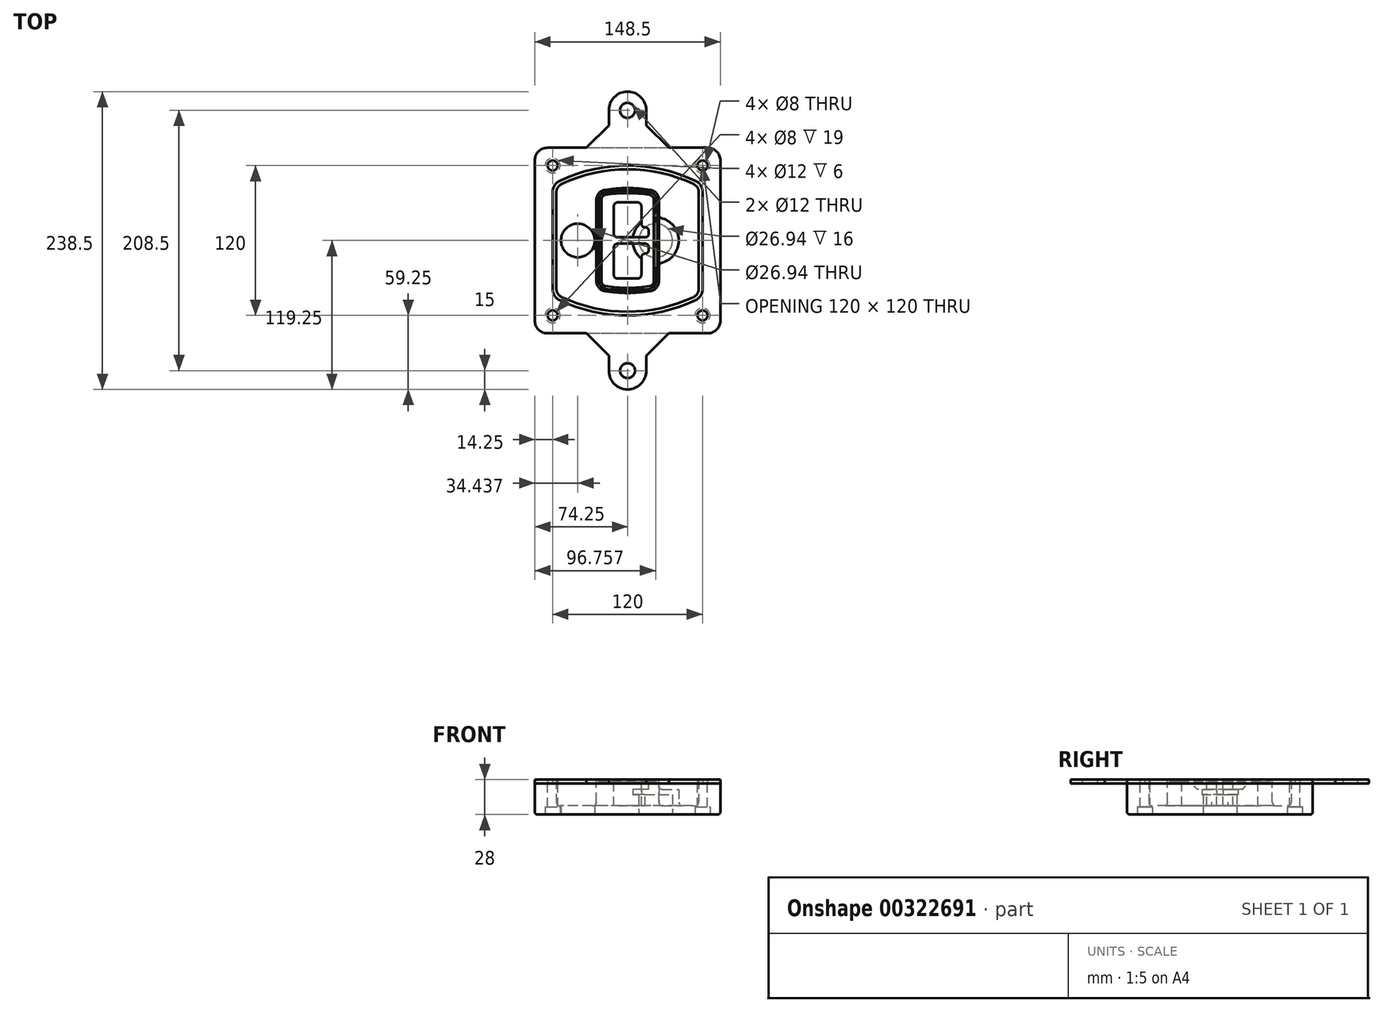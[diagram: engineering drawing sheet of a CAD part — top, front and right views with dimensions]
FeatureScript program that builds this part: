
annotation { "Feature Type Name" : "Feature", "Feature Type Description" : "" }
export const myFeature = defineFeature(function(context is Context, id is Id, definition is map)
    precondition{}
    {
        {
            var Q0;
            Q0=qCreatedBy(makeId("Top.planeOp"),FACE);
            var sketch = newSketch(context, id + "F0", { "sketchPlane" : qUnion([Q0])});
            skPoint(sketch, "E0.rect.middle", {"position": v(0, 0) * mm});
            skLineSegment(sketch, "E1.bottom", {"start": v(-64.25, -74.25) * mm, "end": v(64.25, -74.25) * mm});
            skLineSegment(sketch, "E1.top", {"start": v(-64.25, 74.25) * mm, "end": v(64.25, 74.25) * mm});
            skLineSegment(sketch, "E1.left", {"start": v(-74.25, -64.25) * mm, "end": v(-74.25, 64.25) * mm});
            skLineSegment(sketch, "E1.right", {"start": v(74.25, -64.25) * mm, "end": v(74.25, 64.25) * mm});
            skLineSegment(sketch, "E2", {"start": v(-74.25, 74.25) * mm, "end": v(74.25, -74.25) * mm, "construction": true});
            skLineSegment(sketch, "E3", {"start": v(74.25, 74.25) * mm, "end": v(-74.25, -74.25) * mm, "construction": true});
            skCircle(sketch, "E4", {"center": v(-60, 60) * mm, "radius": 4 * mm});
            skCircle(sketch, "E5", {"center": v(60, 60) * mm, "radius": 4 * mm});
            skCircle(sketch, "E6", {"center": v(60, -60) * mm, "radius": 4 * mm});
            skCircle(sketch, "E7", {"center": v(-60, -60) * mm, "radius": 4 * mm});
            skLineSegment(sketch, "E8", {"start": v(-60, 60) * mm, "end": v(60, 60) * mm, "construction": true});
            skLineSegment(sketch, "E9", {"start": v(60, 60) * mm, "end": v(60, -60) * mm, "construction": true});
            skLineSegment(sketch, "E10", {"start": v(60, -60) * mm, "end": v(-60, -60) * mm, "construction": true});
            skLineSegment(sketch, "E11", {"start": v(-60, -60) * mm, "end": v(-60, 60) * mm, "construction": true});
            skLineSegment(sketch, "E12", {"start": v(-60, 38.83) * mm, "end": v(-60, -38.83) * mm});
            skLineSegment(sketch, "E13", {"start": v(60, 38.83) * mm, "end": v(60, -38.83) * mm});
            skArc(sketch, "E14", {"start": v(54.26, 47.88) * mm, "mid": v(0, 60) * mm, "end": v(-54.26, 47.88) * mm});
            skArc(sketch, "E15", {"start": v(-54.26, -47.88) * mm, "mid": v(0, -60) * mm, "end": v(54.26, -47.88) * mm});
            skLineSegment(sketch, "E16", {"start": v(-60, 0) * mm, "end": v(60, 0) * mm, "construction": true});
            skPoint(sketch, "E17.visualSharp", {"position": v(-60, -45) * mm});
            skArc(sketch, "E17.filletArc", {"start": v(-60, -38.83) * mm, "mid": v(-58.44, -44.2) * mm, "end": v(-54.26, -47.88) * mm});
            skPoint(sketch, "E18.visualSharp", {"position": v(-60, 45) * mm});
            skArc(sketch, "E18.filletArc", {"start": v(-54.26, 47.88) * mm, "mid": v(-58.44, 44.2) * mm, "end": v(-60, 38.83) * mm});
            skPoint(sketch, "E19.visualSharp", {"position": v(60, 45) * mm});
            skArc(sketch, "E19.filletArc", {"start": v(60, 38.83) * mm, "mid": v(58.44, 44.2) * mm, "end": v(54.26, 47.88) * mm});
            skPoint(sketch, "E20.visualSharp", {"position": v(60, -45) * mm});
            skArc(sketch, "E20.filletArc", {"start": v(54.26, -47.88) * mm, "mid": v(58.44, -44.2) * mm, "end": v(60, -38.83) * mm});
            skPoint(sketch, "E21.visualSharp", {"position": v(-74.25, 74.25) * mm});
            skArc(sketch, "E21.filletArc", {"start": v(-64.25, 74.25) * mm, "mid": v(-71.32, 71.32) * mm, "end": v(-74.25, 64.25) * mm});
            skPoint(sketch, "E22.visualSharp", {"position": v(74.25, 74.25) * mm});
            skArc(sketch, "E22.filletArc", {"start": v(74.25, 64.25) * mm, "mid": v(71.32, 71.32) * mm, "end": v(64.25, 74.25) * mm});
            skPoint(sketch, "E23.visualSharp", {"position": v(74.25, -74.25) * mm});
            skArc(sketch, "E23.filletArc", {"start": v(64.25, -74.25) * mm, "mid": v(71.32, -71.32) * mm, "end": v(74.25, -64.25) * mm});
            skPoint(sketch, "E24.visualSharp", {"position": v(-74.25, -74.25) * mm});
            skArc(sketch, "E24.filletArc", {"start": v(-74.25, -64.25) * mm, "mid": v(-71.32, -71.32) * mm, "end": v(-64.25, -74.25) * mm});
            skArc(sketch, "E25.0", {"start": v(57, 38.83) * mm, "mid": v(55.9, 42.58) * mm, "end": v(52.98, 45.17) * mm});
            skLineSegment(sketch, "E25.1", {"start": v(57, 38.83) * mm, "end": v(57, -38.83) * mm});
            skArc(sketch, "E25.2", {"start": v(52.98, -45.17) * mm, "mid": v(55.9, -42.58) * mm, "end": v(57, -38.83) * mm});
            skArc(sketch, "E25.3", {"start": v(-52.98, -45.17) * mm, "mid": v(0, -57) * mm, "end": v(52.98, -45.17) * mm});
            skArc(sketch, "E25.4", {"start": v(-57, -38.83) * mm, "mid": v(-55.9, -42.58) * mm, "end": v(-52.98, -45.17) * mm});
            skArc(sketch, "E25.5", {"start": v(52.98, 45.17) * mm, "mid": v(0, 57) * mm, "end": v(-52.98, 45.17) * mm});
            skLineSegment(sketch, "E25.6", {"start": v(-57, 38.83) * mm, "end": v(-57, -38.83) * mm});
            skArc(sketch, "E25.7", {"start": v(-52.98, 45.17) * mm, "mid": v(-55.9, 42.58) * mm, "end": v(-57, 38.83) * mm});
            skArc(sketch, "E26.0", {"start": v(-55.96, 51.5) * mm, "mid": v(-61.82, 46.33) * mm, "end": v(-64, 38.83) * mm});
            skArc(sketch, "E26.1", {"start": v(55.96, 51.5) * mm, "mid": v(0, 64) * mm, "end": v(-55.96, 51.5) * mm});
            skArc(sketch, "E26.2", {"start": v(64, 38.83) * mm, "mid": v(61.82, 46.33) * mm, "end": v(55.96, 51.5) * mm});
            skLineSegment(sketch, "E26.3", {"start": v(64, 38.83) * mm, "end": v(64, -38.83) * mm});
            skArc(sketch, "E26.4", {"start": v(55.96, -51.5) * mm, "mid": v(61.82, -46.33) * mm, "end": v(64, -38.83) * mm});
            skLineSegment(sketch, "E26.5", {"start": v(-64, 38.83) * mm, "end": v(-64, -38.83) * mm});
            skArc(sketch, "E26.6", {"start": v(-55.96, -51.5) * mm, "mid": v(0, -64) * mm, "end": v(55.96, -51.5) * mm});
            skArc(sketch, "E26.7", {"start": v(-64, -38.83) * mm, "mid": v(-61.82, -46.33) * mm, "end": v(-55.96, -51.5) * mm});
            skSolve(sketch);
        }
        {
            var Q0;
            Q0=makeQuery(id+"F0.imprint","IMPRINT",FACE,{"disambiguationData":[TD([[makeQuery(id+"F0.imprint","IMPRINT",EDGE,{"derivedFrom":sQuery(id+"F0.wireOp",EDGE,"E1.bottom")}),1.0]])]});
            var Q1;
            Q1=makeQuery(id+"F0.imprint","IMPRINT",FACE,{"disambiguationData":[TD([[makeQuery(id+"F0.imprint","IMPRINT",EDGE,{"derivedFrom":sQuery(id+"F0.wireOp",EDGE,"E12")}),1.0]])]});
            var Q2;
            Q2=makeQuery(id+"F0.imprint","IMPRINT",FACE,{"disambiguationData":[TD([[makeQuery(id+"F0.imprint","IMPRINT",EDGE,{"derivedFrom":sQuery(id+"F0.wireOp",EDGE,"E25.0")}),1.0]])]});
            var Q3;
            Q3=makeQuery(id+"F0.imprint","IMPRINT",FACE,{"disambiguationData":[TD([[makeQuery(id+"F0.imprint","IMPRINT",EDGE,{"derivedFrom":sQuery(id+"F0.wireOp",EDGE,"E12")}),-1.0]])]});
            extrude(context, id + "F1", {"entities" : qUnion([Q0, Q1, Q2, Q3]), "oppositeDirection" : true, "depth" : 25 * mm});
        }
        {
            var Q0;
            Q0=makeQuery(id+"F0.imprint","IMPRINT",FACE,{"disambiguationData":[TD([[makeQuery(id+"F0.imprint","IMPRINT",EDGE,{"derivedFrom":sQuery(id+"F0.wireOp",EDGE,"E12")}),1.0]])]});
            extrude(context, id + "F2", {"entities" : qUnion([Q0]), "operationType" : NewBodyOperationType.ADD, "depth" : 3 * mm});
        }
        {
            var Q0;
            Q0=makeQuery(id+"F0.imprint","IMPRINT",FACE,{"disambiguationData":[TD([[makeQuery(id+"F0.imprint","IMPRINT",EDGE,{"derivedFrom":sQuery(id+"F0.wireOp",EDGE,"E25.0")}),1.0]])]});
            extrude(context, id + "F3", {"entities" : qUnion([Q0]), "operationType" : NewBodyOperationType.REMOVE, "oppositeDirection" : true, "depth" : 18 * mm});
        }
        {
            var Q0;
            Q0=makeQuery(id+"F2.opExtrude","CAP_FACE",FACE,{"disambiguationData":[OSD([sQuery(id+"F0.wireOp",EDGE,"E12"),sQuery(id+"F0.wireOp",EDGE,"E13"),sQuery(id+"F0.wireOp",EDGE,"E14"),sQuery(id+"F0.wireOp",EDGE,"E15"),sQuery(id+"F0.wireOp",EDGE,"E17.filletArc"),sQuery(id+"F0.wireOp",EDGE,"E18.filletArc"),sQuery(id+"F0.wireOp",EDGE,"E19.filletArc"),sQuery(id+"F0.wireOp",EDGE,"E20.filletArc"),sQuery(id+"F0.wireOp",EDGE,"E25.0"),sQuery(id+"F0.wireOp",EDGE,"E25.1"),sQuery(id+"F0.wireOp",EDGE,"E25.2"),sQuery(id+"F0.wireOp",EDGE,"E25.3"),sQuery(id+"F0.wireOp",EDGE,"E25.4"),sQuery(id+"F0.wireOp",EDGE,"E25.5"),sQuery(id+"F0.wireOp",EDGE,"E25.6"),sQuery(id+"F0.wireOp",EDGE,"E25.7")])],"isStart":false});
            var sketch = newSketch(context, id + "F4", { "sketchPlane" : qUnion([Q0])});
            skArc(sketch, "E27.0", {"start": v(-18.34, -40.45) * mm, "mid": v(0, -42) * mm, "end": v(18.34, -40.45) * mm});
            skArc(sketch, "E28.0", {"start": v(18.34, 40.45) * mm, "mid": v(0, 42) * mm, "end": v(-18.34, 40.45) * mm});
            skLineSegment(sketch, "E29", {"start": v(-25, 32.57) * mm, "end": v(-25, -32.57) * mm});
            skLineSegment(sketch, "E30", {"start": v(25, 32.57) * mm, "end": v(25, -32.57) * mm});
            skLineSegment(sketch, "E31", {"start": v(-25, 39.1) * mm, "end": v(25, 39.1) * mm, "construction": true});
            skLineSegment(sketch, "E32", {"start": v(-25, -39.1) * mm, "end": v(25, -39.1) * mm, "construction": true});
            skPoint(sketch, "E33.visualSharp", {"position": v(-25, 39.1) * mm});
            skArc(sketch, "E33.filletArc", {"start": v(-18.34, 40.45) * mm, "mid": v(-23.11, 37.73) * mm, "end": v(-25, 32.57) * mm});
            skPoint(sketch, "E34.visualSharp", {"position": v(25, 39.1) * mm});
            skArc(sketch, "E34.filletArc", {"start": v(25, 32.57) * mm, "mid": v(23.11, 37.73) * mm, "end": v(18.34, 40.45) * mm});
            skPoint(sketch, "E35.visualSharp", {"position": v(25, -39.1) * mm});
            skArc(sketch, "E35.filletArc", {"start": v(18.34, -40.45) * mm, "mid": v(23.11, -37.73) * mm, "end": v(25, -32.57) * mm});
            skPoint(sketch, "E36.visualSharp", {"position": v(-25, -39.1) * mm});
            skArc(sketch, "E36.filletArc", {"start": v(-25, -32.57) * mm, "mid": v(-23.11, -37.73) * mm, "end": v(-18.34, -40.45) * mm});
            skArc(sketch, "E37.0", {"start": v(52.98, 45.17) * mm, "mid": v(0, 57) * mm, "end": v(-52.98, 45.17) * mm});
            skArc(sketch, "E37.1", {"start": v(-52.98, 45.17) * mm, "mid": v(-55.9, 42.58) * mm, "end": v(-57, 38.83) * mm});
            skLineSegment(sketch, "E37.2", {"start": v(-57, 38.83) * mm, "end": v(-57, -38.83) * mm});
            skArc(sketch, "E37.3", {"start": v(-57, -38.83) * mm, "mid": v(-55.9, -42.58) * mm, "end": v(-52.98, -45.17) * mm});
            skArc(sketch, "E37.4", {"start": v(-52.98, -45.17) * mm, "mid": v(0, -57) * mm, "end": v(52.98, -45.17) * mm});
            skArc(sketch, "E37.5", {"start": v(52.98, -45.17) * mm, "mid": v(55.9, -42.58) * mm, "end": v(57, -38.83) * mm});
            skLineSegment(sketch, "E37.6", {"start": v(57, 38.83) * mm, "end": v(57, -38.83) * mm});
            skArc(sketch, "E37.7", {"start": v(57, 38.83) * mm, "mid": v(55.9, 42.58) * mm, "end": v(52.98, 45.17) * mm});
            skLineSegment(sketch, "E38.0", {"start": v(23, 32.57) * mm, "end": v(23, -32.57) * mm});
            skArc(sketch, "E38.1", {"start": v(18, -38.48) * mm, "mid": v(21.58, -36.44) * mm, "end": v(23, -32.57) * mm});
            skArc(sketch, "E38.2", {"start": v(-18, -38.48) * mm, "mid": v(0, -40) * mm, "end": v(18, -38.48) * mm});
            skArc(sketch, "E38.3", {"start": v(-23, -32.57) * mm, "mid": v(-21.58, -36.44) * mm, "end": v(-18, -38.48) * mm});
            skLineSegment(sketch, "E38.4", {"start": v(-23, 32.57) * mm, "end": v(-23, -32.57) * mm});
            skArc(sketch, "E38.5", {"start": v(23, 32.57) * mm, "mid": v(21.58, 36.44) * mm, "end": v(18, 38.48) * mm});
            skArc(sketch, "E38.6", {"start": v(-18, 38.48) * mm, "mid": v(-21.58, 36.44) * mm, "end": v(-23, 32.57) * mm});
            skArc(sketch, "E38.7", {"start": v(18, 38.48) * mm, "mid": v(0, 40) * mm, "end": v(-18, 38.48) * mm});
            skArc(sketch, "E39.0", {"start": v(21, 32.57) * mm, "mid": v(20.06, 35.15) * mm, "end": v(17.67, 36.5) * mm});
            skLineSegment(sketch, "E39.1", {"start": v(21, 32.57) * mm, "end": v(21, -32.57) * mm});
            skArc(sketch, "E39.2", {"start": v(17.67, -36.5) * mm, "mid": v(20.06, -35.15) * mm, "end": v(21, -32.57) * mm});
            skArc(sketch, "E39.3", {"start": v(-17.67, -36.5) * mm, "mid": v(0, -38) * mm, "end": v(17.67, -36.5) * mm});
            skArc(sketch, "E39.4", {"start": v(-21, -32.57) * mm, "mid": v(-20.06, -35.15) * mm, "end": v(-17.67, -36.5) * mm});
            skArc(sketch, "E39.5", {"start": v(17.67, 36.5) * mm, "mid": v(0, 38) * mm, "end": v(-17.67, 36.5) * mm});
            skLineSegment(sketch, "E39.6", {"start": v(-21, 32.57) * mm, "end": v(-21, -32.57) * mm});
            skArc(sketch, "E39.7", {"start": v(-17.67, 36.5) * mm, "mid": v(-20.06, 35.15) * mm, "end": v(-21, 32.57) * mm});
            skLineSegment(sketch, "E40", {"start": v(-25, 0) * mm, "end": v(25, 0) * mm, "construction": true});
            skLineSegment(sketch, "E41", {"start": v(-11, 5.5) * mm, "end": v(-11, 27.5) * mm});
            skLineSegment(sketch, "E42", {"start": v(-8, 30.5) * mm, "end": v(8, 30.5) * mm});
            skLineSegment(sketch, "E43", {"start": v(11, 27.5) * mm, "end": v(11, 13.5) * mm});
            skLineSegment(sketch, "E44", {"start": v(14, 10.5) * mm, "end": v(14, 10.5) * mm});
            skLineSegment(sketch, "E45", {"start": v(17, 7.5) * mm, "end": v(17, 5.5) * mm});
            skLineSegment(sketch, "E46", {"start": v(14, 2.5) * mm, "end": v(-8, 2.5) * mm});
            skPoint(sketch, "E47.visualSharp", {"position": v(-11, 30.5) * mm});
            skArc(sketch, "E47.filletArc", {"start": v(-8, 30.5) * mm, "mid": v(-10.12, 29.62) * mm, "end": v(-11, 27.5) * mm});
            skPoint(sketch, "E48.visualSharp", {"position": v(11, 30.5) * mm});
            skArc(sketch, "E48.filletArc", {"start": v(11, 27.5) * mm, "mid": v(10.12, 29.62) * mm, "end": v(8, 30.5) * mm});
            skPoint(sketch, "E49.visualSharp", {"position": v(11, 10.5) * mm});
            skArc(sketch, "E49.filletArc", {"start": v(11, 13.5) * mm, "mid": v(11.88, 11.38) * mm, "end": v(14, 10.5) * mm});
            skPoint(sketch, "E50.visualSharp", {"position": v(17, 10.5) * mm});
            skArc(sketch, "E50.filletArc", {"start": v(17, 7.5) * mm, "mid": v(16.12, 9.62) * mm, "end": v(14, 10.5) * mm});
            skPoint(sketch, "E51.visualSharp", {"position": v(17, 2.5) * mm});
            skArc(sketch, "E51.filletArc", {"start": v(14, 2.5) * mm, "mid": v(16.12, 3.38) * mm, "end": v(17, 5.5) * mm});
            skPoint(sketch, "E52.visualSharp", {"position": v(-11, 2.5) * mm});
            skArc(sketch, "E52.filletArc", {"start": v(-11, 5.5) * mm, "mid": v(-10.12, 3.38) * mm, "end": v(-8, 2.5) * mm});
            skLineSegment(sketch, "E53.0.MirrorCS", {"start": v(14, -2.5) * mm, "end": v(-8, -2.5) * mm});
            skArc(sketch, "E54.0.MirrorCS", {"start": v(-11, -5.5) * mm, "mid": v(-10.12, -3.38) * mm, "end": v(-8, -2.5) * mm});
            skLineSegment(sketch, "E55.0.MirrorCS", {"start": v(-11, -5.5) * mm, "end": v(-11, -27.5) * mm});
            skArc(sketch, "E56.0.MirrorCS", {"start": v(-8, -30.5) * mm, "mid": v(-10.12, -29.62) * mm, "end": v(-11, -27.5) * mm});
            skLineSegment(sketch, "E57.0.MirrorCS", {"start": v(-8, -30.5) * mm, "end": v(8, -30.5) * mm});
            skArc(sketch, "E58.0.MirrorCS", {"start": v(11, -27.5) * mm, "mid": v(10.12, -29.62) * mm, "end": v(8, -30.5) * mm});
            skLineSegment(sketch, "E59.0.MirrorCS", {"start": v(11, -27.5) * mm, "end": v(11, -13.5) * mm});
            skArc(sketch, "E60.0.MirrorCS", {"start": v(11, -13.5) * mm, "mid": v(11.88, -11.38) * mm, "end": v(14, -10.5) * mm});
            skArc(sketch, "E61.0.MirrorCS", {"start": v(17, -7.5) * mm, "mid": v(16.12, -9.62) * mm, "end": v(14, -10.5) * mm});
            skLineSegment(sketch, "E62.0.MirrorCS", {"start": v(17, -7.5) * mm, "end": v(17, -5.5) * mm});
            skArc(sketch, "E63.0.MirrorCS", {"start": v(14, -2.5) * mm, "mid": v(16.12, -3.38) * mm, "end": v(17, -5.5) * mm});
            skSolve(sketch);
        }
        {
            var Q0;
            Q0=makeQuery(id+"F4.imprint","IMPRINT",FACE,{"disambiguationData":[TD([[makeQuery(id+"F4.imprint","IMPRINT",EDGE,{"derivedFrom":sQuery(id+"F4.wireOp",EDGE,"E27.0")}),1.0]])]});
            var Q1;
            Q1=makeQuery(id+"F4.imprint","IMPRINT",FACE,{"disambiguationData":[TD([[makeQuery(id+"F4.imprint","IMPRINT",EDGE,{"derivedFrom":sQuery(id+"F4.wireOp",EDGE,"E38.0")}),-1.0]])]});
            var Q2;
            Q2=makeQuery(id+"F4.imprint","IMPRINT",FACE,{"disambiguationData":[TD([[makeQuery(id+"F4.imprint","IMPRINT",EDGE,{"derivedFrom":sQuery(id+"F4.wireOp",EDGE,"E39.0")}),1.0]])]});
            extrude(context, id + "F5", {"entities" : qUnion([Q0, Q1, Q2]), "operationType" : NewBodyOperationType.ADD, "endBound" : BoundingType.UP_TO_NEXT, "oppositeDirection" : true, "depth" : 25 * mm});
        }
        {
            var Q0;
            Q0=makeQuery(id+"F4.imprint","IMPRINT",FACE,{"disambiguationData":[TD([[makeQuery(id+"F4.imprint","IMPRINT",EDGE,{"derivedFrom":sQuery(id+"F4.wireOp",EDGE,"E38.0")}),-1.0]])]});
            extrude(context, id + "F6", {"entities" : qUnion([Q0]), "operationType" : NewBodyOperationType.REMOVE, "oppositeDirection" : true, "depth" : 2 * mm});
        }
        {
            var Q0;
            Q0=makeQuery(id+"F1.opExtrude","CAP_FACE",FACE,{"disambiguationData":[OSD([sQuery(id+"F0.wireOp",EDGE,"E1.bottom"),sQuery(id+"F0.wireOp",EDGE,"E1.top"),sQuery(id+"F0.wireOp",EDGE,"E1.left"),sQuery(id+"F0.wireOp",EDGE,"E1.right"),sQuery(id+"F0.wireOp",EDGE,"E4"),sQuery(id+"F0.wireOp",EDGE,"E5"),sQuery(id+"F0.wireOp",EDGE,"E6"),sQuery(id+"F0.wireOp",EDGE,"E7"),sQuery(id+"F0.wireOp",EDGE,"E21.filletArc"),sQuery(id+"F0.wireOp",EDGE,"E22.filletArc"),sQuery(id+"F0.wireOp",EDGE,"E23.filletArc"),sQuery(id+"F0.wireOp",EDGE,"E24.filletArc")])],"isStart":false});
            var sketch = newSketch(context, id + "F7", { "sketchPlane" : qUnion([Q0])});
            skCircle(sketch, "E64", {"center": v(22.5, 0) * mm, "radius": 13.47 * mm});
            skCircle(sketch, "E65", {"center": v(-39.81, 0) * mm, "radius": 13.47 * mm});
            skLineSegment(sketch, "E66", {"start": v(74.25, 0) * mm, "end": v(-74.25, 0) * mm});
            skCircle(sketch, "E67", {"center": v(22.5, 0) * mm, "radius": 18.47 * mm});
            skCircle(sketch, "E68", {"center": v(60, -60) * mm, "radius": 6 * mm});
            skCircle(sketch, "E69", {"center": v(-60, -60) * mm, "radius": 6 * mm});
            skCircle(sketch, "E70", {"center": v(-60, 60) * mm, "radius": 6 * mm});
            skCircle(sketch, "E71", {"center": v(60, 60) * mm, "radius": 6 * mm});
            skSolve(sketch);
        }
        {
            var Q0;
            {var subQ1=sQuery(id+"F7.wireOp",EDGE,"E66");var subQ4=sQuery(id+"F7.wireOp",EDGE,"E64");var subQ6=makeQuery(id+"F7.imprint","INTERSECT",VERTEX,{"disambiguationData":[OD(0.0)],"derivedFrom":[subQ4,subQ1]});Q0=makeQuery(id+"F7.imprint","IMPRINT",FACE,{"disambiguationData":[TD([[makeQuery(id+"F7.imprint","IMPRINT",EDGE,{"disambiguationData":[TD([[subQ6,-1.0]])],"derivedFrom":subQ4}),-1.0]])]});}
            var Q1;
            {var subQ0=sQuery(id+"F7.wireOp",EDGE,"E66");var subQ1=sQuery(id+"F7.wireOp",EDGE,"E64");var subQ3=makeQuery(id+"F7.imprint","INTERSECT",VERTEX,{"disambiguationData":[OD(0.0)],"derivedFrom":[subQ1,subQ0]});Q1=makeQuery(id+"F7.imprint","IMPRINT",FACE,{"disambiguationData":[TD([[makeQuery(id+"F7.imprint","IMPRINT",EDGE,{"disambiguationData":[TD([[subQ3,-1.0]])],"derivedFrom":subQ1}),1.0]])]});}
            var Q2;
            {var subQ0=sQuery(id+"F7.wireOp",EDGE,"E66");var subQ1=sQuery(id+"F7.wireOp",EDGE,"E64");var subQ3=makeQuery(id+"F7.imprint","INTERSECT",VERTEX,{"disambiguationData":[OD(0.0)],"derivedFrom":[subQ1,subQ0]});Q2=makeQuery(id+"F7.imprint","IMPRINT",FACE,{"disambiguationData":[TD([[makeQuery(id+"F7.imprint","IMPRINT",EDGE,{"disambiguationData":[TD([[subQ3,1.0]])],"derivedFrom":subQ1}),1.0]])]});}
            var Q3;
            {var subQ1=sQuery(id+"F7.wireOp",EDGE,"E66");var subQ4=sQuery(id+"F7.wireOp",EDGE,"E64");var subQ6=makeQuery(id+"F7.imprint","INTERSECT",VERTEX,{"disambiguationData":[OD(0.0)],"derivedFrom":[subQ4,subQ1]});Q3=makeQuery(id+"F7.imprint","IMPRINT",FACE,{"disambiguationData":[TD([[makeQuery(id+"F7.imprint","IMPRINT",EDGE,{"disambiguationData":[TD([[subQ6,1.0]])],"derivedFrom":subQ4}),-1.0]])]});}
            extrude(context, id + "F8", {"entities" : qUnion([Q0, Q1, Q2, Q3]), "operationType" : NewBodyOperationType.ADD, "oppositeDirection" : true, "depth" : 20 * mm});
        }
        {
            var Q0;
            {var subQ0=sQuery(id+"F7.wireOp",EDGE,"E66");var subQ1=sQuery(id+"F7.wireOp",EDGE,"E64");var subQ3=makeQuery(id+"F7.imprint","INTERSECT",VERTEX,{"disambiguationData":[OD(0.0)],"derivedFrom":[subQ1,subQ0]});Q0=makeQuery(id+"F7.imprint","IMPRINT",FACE,{"disambiguationData":[TD([[makeQuery(id+"F7.imprint","IMPRINT",EDGE,{"disambiguationData":[TD([[subQ3,-1.0]])],"derivedFrom":subQ1}),1.0]])]});}
            var Q1;
            {var subQ0=sQuery(id+"F7.wireOp",EDGE,"E66");var subQ1=sQuery(id+"F7.wireOp",EDGE,"E64");var subQ3=makeQuery(id+"F7.imprint","INTERSECT",VERTEX,{"disambiguationData":[OD(0.0)],"derivedFrom":[subQ1,subQ0]});Q1=makeQuery(id+"F7.imprint","IMPRINT",FACE,{"disambiguationData":[TD([[makeQuery(id+"F7.imprint","IMPRINT",EDGE,{"disambiguationData":[TD([[subQ3,1.0]])],"derivedFrom":subQ1}),1.0]])]});}
            extrude(context, id + "F9", {"entities" : qUnion([Q0, Q1]), "operationType" : NewBodyOperationType.REMOVE, "oppositeDirection" : true, "depth" : 16 * mm});
        }
        {
            var Q0;
            {var subQ0=sQuery(id+"F7.wireOp",EDGE,"E66");var subQ1=sQuery(id+"F7.wireOp",EDGE,"E65");var subQ3=makeQuery(id+"F7.imprint","INTERSECT",VERTEX,{"disambiguationData":[OD(0.0)],"derivedFrom":[subQ1,subQ0]});Q0=makeQuery(id+"F7.imprint","IMPRINT",FACE,{"disambiguationData":[TD([[makeQuery(id+"F7.imprint","IMPRINT",EDGE,{"disambiguationData":[TD([[subQ3,-1.0]])],"derivedFrom":subQ1}),1.0]])]});}
            var Q1;
            {var subQ0=sQuery(id+"F7.wireOp",EDGE,"E66");var subQ1=sQuery(id+"F7.wireOp",EDGE,"E65");var subQ3=makeQuery(id+"F7.imprint","INTERSECT",VERTEX,{"disambiguationData":[OD(0.0)],"derivedFrom":[subQ1,subQ0]});Q1=makeQuery(id+"F7.imprint","IMPRINT",FACE,{"disambiguationData":[TD([[makeQuery(id+"F7.imprint","IMPRINT",EDGE,{"disambiguationData":[TD([[subQ3,1.0]])],"derivedFrom":subQ1}),1.0]])]});}
            extrude(context, id + "F10", {"entities" : qUnion([Q0, Q1]), "operationType" : NewBodyOperationType.REMOVE, "oppositeDirection" : true, "depth" : 25 * mm});
        }
        {
            var Q0;
            Q0=makeQuery(id+"F7.imprint","IMPRINT",FACE,{"disambiguationData":[TD([[makeQuery(id+"F7.imprint","IMPRINT",EDGE,{"derivedFrom":sQuery(id+"F7.wireOp",EDGE,"E68")}),1.0]])]});
            var Q1;
            Q1=makeQuery(id+"F7.imprint","IMPRINT",FACE,{"disambiguationData":[TD([[makeQuery(id+"F7.imprint","IMPRINT",EDGE,{"derivedFrom":makeQuery(id+"F1.opExtrude","CAP_EDGE",EDGE,{"disambiguationData":[OSD([sQuery(id+"F0.wireOp",EDGE,"E5")])],"isStart":false})}),-1.0]])]});
            var Q2;
            Q2=makeQuery(id+"F7.imprint","IMPRINT",FACE,{"disambiguationData":[TD([[makeQuery(id+"F7.imprint","IMPRINT",EDGE,{"derivedFrom":sQuery(id+"F7.wireOp",EDGE,"E69")}),1.0]])]});
            var Q3;
            Q3=makeQuery(id+"F7.imprint","IMPRINT",FACE,{"disambiguationData":[TD([[makeQuery(id+"F7.imprint","IMPRINT",EDGE,{"derivedFrom":makeQuery(id+"F1.opExtrude","CAP_EDGE",EDGE,{"disambiguationData":[OSD([sQuery(id+"F0.wireOp",EDGE,"E4")])],"isStart":false})}),-1.0]])]});
            var Q4;
            Q4=makeQuery(id+"F7.imprint","IMPRINT",FACE,{"disambiguationData":[TD([[makeQuery(id+"F7.imprint","IMPRINT",EDGE,{"derivedFrom":sQuery(id+"F7.wireOp",EDGE,"E70")}),1.0]])]});
            var Q5;
            Q5=makeQuery(id+"F7.imprint","IMPRINT",FACE,{"disambiguationData":[TD([[makeQuery(id+"F7.imprint","IMPRINT",EDGE,{"derivedFrom":makeQuery(id+"F1.opExtrude","CAP_EDGE",EDGE,{"disambiguationData":[OSD([sQuery(id+"F0.wireOp",EDGE,"E7")])],"isStart":false})}),-1.0]])]});
            var Q6;
            Q6=makeQuery(id+"F7.imprint","IMPRINT",FACE,{"disambiguationData":[TD([[makeQuery(id+"F7.imprint","IMPRINT",EDGE,{"derivedFrom":sQuery(id+"F7.wireOp",EDGE,"E71")}),1.0]])]});
            var Q7;
            Q7=makeQuery(id+"F7.imprint","IMPRINT",FACE,{"disambiguationData":[TD([[makeQuery(id+"F7.imprint","IMPRINT",EDGE,{"derivedFrom":makeQuery(id+"F1.opExtrude","CAP_EDGE",EDGE,{"disambiguationData":[OSD([sQuery(id+"F0.wireOp",EDGE,"E6")])],"isStart":false})}),-1.0]])]});
            extrude(context, id + "F11", {"entities" : qUnion([Q0, Q1, Q2, Q3, Q4, Q5, Q6, Q7]), "operationType" : NewBodyOperationType.REMOVE, "oppositeDirection" : true, "depth" : 6 * mm});
        }
        {
            var Q0;
            Q0=makeQuery(id+"F9.boolean.opBoolean","COPY",FACE,{"derivedFrom":makeQuery(id+"F9.opExtrude","CAP_FACE",FACE,{"disambiguationData":[OSD([sQuery(id+"F7.wireOp",EDGE,"E64")])],"isStart":false})});
            var sketch = newSketch(context, id + "F12", { "sketchPlane" : qUnion([Q0])});
            skArc(sketch, "E72.0", {"start": v(11, 14.45) * mm, "mid": v(6.45, 9.13) * mm, "end": v(4.2, 2.5) * mm});
            skArc(sketch, "E72.1", {"start": v(4.2, -2.5) * mm, "mid": v(6.45, -9.13) * mm, "end": v(11, -14.45) * mm});
            skLineSegment(sketch, "E73", {"start": v(4.2, -2.5) * mm, "end": v(14, -2.5) * mm});
            skLineSegment(sketch, "E74.0", {"start": v(14, 2.5) * mm, "end": v(4.2, 2.5) * mm});
            skArc(sketch, "E74.1", {"start": v(14, 2.5) * mm, "mid": v(16.12, 3.38) * mm, "end": v(17, 5.5) * mm});
            skLineSegment(sketch, "E74.2", {"start": v(17, 7.5) * mm, "end": v(17, 5.5) * mm});
            skArc(sketch, "E74.3", {"start": v(17, 7.5) * mm, "mid": v(16.12, 9.62) * mm, "end": v(14, 10.5) * mm});
            skArc(sketch, "E74.4", {"start": v(11, 13.5) * mm, "mid": v(11.88, 11.38) * mm, "end": v(14, 10.5) * mm});
            skLineSegment(sketch, "E74.5", {"start": v(11, 14.45) * mm, "end": v(11, 13.5) * mm});
            skLineSegment(sketch, "E74.7", {"start": v(14, -2.5) * mm, "end": v(4.2, -2.5) * mm});
            skArc(sketch, "E74.8", {"start": v(14, -2.5) * mm, "mid": v(16.12, -3.38) * mm, "end": v(17, -5.5) * mm});
            skLineSegment(sketch, "E74.9", {"start": v(17, -7.5) * mm, "end": v(17, -5.5) * mm});
            skArc(sketch, "E74.10", {"start": v(17, -7.5) * mm, "mid": v(16.12, -9.62) * mm, "end": v(14, -10.5) * mm});
            skArc(sketch, "E74.11", {"start": v(11, -13.5) * mm, "mid": v(11.88, -11.38) * mm, "end": v(14, -10.5) * mm});
            skLineSegment(sketch, "E74.12", {"start": v(11, -14.45) * mm, "end": v(11, -13.5) * mm});
            skPoint(sketch, "E75.orphan", {"position": v(11, -27.5) * mm});
            skPoint(sketch, "E76.orphan", {"position": v(-8, -2.5) * mm});
            skPoint(sketch, "E77.orphan", {"position": v(-8, 2.5) * mm});
            skPoint(sketch, "E78.orphan", {"position": v(11, 27.5) * mm});
            skSolve(sketch);
        }
        {
            var Q0;
            {var subQ7=sQuery(id+"F12.wireOp",EDGE,"E72.0");var subQ14=sQuery(id+"F12.wireOp",EDGE,"E72.1");var subQ16=sQuery(id+"F12.wireOp",EDGE,"E74.1");var subQ18=sQuery(id+"F12.wireOp",EDGE,"E74.8");Q0=qUnion([makeQuery(id+"F12.imprint","IMPRINT",FACE,{"disambiguationData":[TD([[makeQuery(id+"F12.imprint","IMPRINT",EDGE,{"derivedFrom":subQ7}),1.0]])]}),makeQuery(id+"F12.imprint","IMPRINT",FACE,{"disambiguationData":[TD([[makeQuery(id+"F12.imprint","IMPRINT",EDGE,{"derivedFrom":subQ14}),1.0]])]}),makeQuery(id+"F12.imprint","IMPRINT",FACE,{"disambiguationData":[TD([[makeQuery(id+"F12.imprint","IMPRINT",EDGE,{"derivedFrom":subQ16}),1.0]])]}),makeQuery(id+"F12.imprint","IMPRINT",FACE,{"disambiguationData":[TD([[makeQuery(id+"F12.imprint","IMPRINT",EDGE,{"derivedFrom":subQ18}),-1.0]])]})]);}
            var Q1;
            Q1=makeQuery(id+"F5.boolean.opBoolean","SPLIT",FACE,{"disambiguationData":[TD([makeQuery(id+"F5.opExtrude","SWEPT_FACE",FACE,{"disambiguationData":[OSD([sQuery(id+"F4.wireOp",EDGE,"E41")])]})])],"derivedFrom":makeQuery(id+"F3.boolean.opBoolean","COPY",FACE,{"derivedFrom":makeQuery(id+"F3.opExtrude","CAP_FACE",FACE,{"disambiguationData":[OSD([sQuery(id+"F0.wireOp",EDGE,"E25.0"),sQuery(id+"F0.wireOp",EDGE,"E25.1"),sQuery(id+"F0.wireOp",EDGE,"E25.2"),sQuery(id+"F0.wireOp",EDGE,"E25.3"),sQuery(id+"F0.wireOp",EDGE,"E25.4"),sQuery(id+"F0.wireOp",EDGE,"E25.5"),sQuery(id+"F0.wireOp",EDGE,"E25.6"),sQuery(id+"F0.wireOp",EDGE,"E25.7")])],"isStart":false})})});
            extrude(context, id + "F13", {"entities" : qUnion([Q0]), "operationType" : NewBodyOperationType.REMOVE, "endBound" : BoundingType.UP_TO_SURFACE, "endBoundEntityFace" : qUnion([Q1]), "depth" : 25 * mm});
        }
        {
            var Q0;
            Q0=makeQuery(id+"F3.boolean.opBoolean","COPY",EDGE,{"derivedFrom":makeQuery(id+"F3.opExtrude","CAP_EDGE",EDGE,{"disambiguationData":[OSD([sQuery(id+"F0.wireOp",EDGE,"E25.6")])],"isStart":false})});
            var Q1;
            Q1=makeQuery(id+"F8.boolean.opBoolean","INTERSECT",EDGE,{"derivedFrom":[makeQuery(id+"F5.opExtrude","SWEPT_FACE",FACE,{"disambiguationData":[OSD([sQuery(id+"F4.wireOp",EDGE,"E30")])]}),makeQuery(id+"F8.opExtrude","CAP_FACE",FACE,{"disambiguationData":[OSD([sQuery(id+"F7.wireOp",EDGE,"E67")])],"isStart":false})]});
            var Q2;
            Q2=makeQuery(id+"F8.boolean.opBoolean","INTERSECT",EDGE,{"disambiguationData":[OD(1.0)],"derivedFrom":[makeQuery(id+"F5.opExtrude","SWEPT_FACE",FACE,{"disambiguationData":[OSD([sQuery(id+"F4.wireOp",EDGE,"E30")])]}),makeQuery(id+"F8.opExtrude","SWEPT_FACE",FACE,{"disambiguationData":[OSD([sQuery(id+"F7.wireOp",EDGE,"E67")])]})]});
            var Q3;
            {var subQ0=sQuery(id+"F4.wireOp",EDGE,"E30");Q3=makeQuery(id+"F8.boolean.opBoolean","SPLIT",EDGE,{"disambiguationData":[TD([makeQuery(id+"F5.opExtrude","SWEPT_FACE",FACE,{"disambiguationData":[OSD([sQuery(id+"F4.wireOp",EDGE,"E35.filletArc")])]})])],"derivedFrom":makeQuery(id+"F5.opExtrude","CAP_EDGE",EDGE,{"disambiguationData":[OSD([subQ0])],"isStart":false})});}
            var Q4;
            {var subQ0=sQuery(id+"F0.wireOp",EDGE,"E25.7");var subQ1=sQuery(id+"F0.wireOp",EDGE,"E25.1");var subQ2=sQuery(id+"F0.wireOp",EDGE,"E25.6");var subQ3=sQuery(id+"F0.wireOp",EDGE,"E25.5");var subQ4=sQuery(id+"F0.wireOp",EDGE,"E25.4");var subQ5=sQuery(id+"F0.wireOp",EDGE,"E25.0");var subQ6=sQuery(id+"F0.wireOp",EDGE,"E25.2");var subQ7=sQuery(id+"F0.wireOp",EDGE,"E25.3");Q4=makeQuery(id+"F8.boolean.opBoolean","INTERSECT",EDGE,{"derivedFrom":[makeQuery(id+"F5.boolean.opBoolean","SPLIT",FACE,{"disambiguationData":[TD([makeQuery(id+"F2.opExtrude","SWEPT_FACE",FACE,{"disambiguationData":[OSD([subQ5])]})])],"derivedFrom":makeQuery(id+"F3.boolean.opBoolean","COPY",FACE,{"derivedFrom":makeQuery(id+"F3.opExtrude","CAP_FACE",FACE,{"disambiguationData":[OSD([subQ5,subQ1,subQ6,subQ7,subQ4,subQ3,subQ2,subQ0])],"isStart":false})})}),makeQuery(id+"F8.opExtrude","SWEPT_FACE",FACE,{"disambiguationData":[OSD([sQuery(id+"F7.wireOp",EDGE,"E67")])]})]});}
            var Q5;
            Q5=makeQuery(id+"F8.boolean.opBoolean","INTERSECT",EDGE,{"disambiguationData":[OD(0.0)],"derivedFrom":[makeQuery(id+"F5.opExtrude","SWEPT_FACE",FACE,{"disambiguationData":[OSD([sQuery(id+"F4.wireOp",EDGE,"E30")])]}),makeQuery(id+"F8.opExtrude","SWEPT_FACE",FACE,{"disambiguationData":[OSD([sQuery(id+"F7.wireOp",EDGE,"E67")])]})]});
            fillet(context, id + "F14", {"entities" : qUnion([Q0, Q1, Q2, Q3, Q4, Q5]), "radius" : 3 * mm, "tangentPropagation" : true, "allowEdgeOverflow" : false});
        }
        {
            var Q0;
            Q0=makeQuery(id+"F1.opExtrude","CAP_EDGE",EDGE,{"disambiguationData":[OSD([sQuery(id+"F0.wireOp",EDGE,"E1.bottom")])],"isStart":false});
            fillet(context, id + "F15", {"entities" : qUnion([Q0]), "radius" : 2 * mm, "tangentPropagation" : true, "allowEdgeOverflow" : false});
        }
        {
            var Q0;
            Q0=qCreatedBy(makeId("Top.planeOp"),FACE);
            var sketch = newSketch(context, id + "F16", { "sketchPlane" : qUnion([Q0])});
            skLineSegment(sketch, "E79.0", {"start": v(-74.25, -64.25) * mm, "end": v(-74.25, 64.25) * mm});
            skArc(sketch, "E79.1", {"start": v(-64.25, 74.25) * mm, "mid": v(-71.32, 71.32) * mm, "end": v(-74.25, 64.25) * mm});
            skLineSegment(sketch, "E79.2", {"start": v(-64.25, 74.25) * mm, "end": v(64.25, 74.25) * mm});
            skArc(sketch, "E79.3", {"start": v(-74.25, -64.25) * mm, "mid": v(-71.32, -71.32) * mm, "end": v(-64.25, -74.25) * mm});
            skLineSegment(sketch, "E79.4", {"start": v(-64.25, -74.25) * mm, "end": v(64.25, -74.25) * mm});
            skArc(sketch, "E79.5", {"start": v(64.25, -74.25) * mm, "mid": v(71.32, -71.32) * mm, "end": v(74.25, -64.25) * mm});
            skLineSegment(sketch, "E79.6", {"start": v(74.25, -64.25) * mm, "end": v(74.25, 64.25) * mm});
            skArc(sketch, "E79.7", {"start": v(74.25, 64.25) * mm, "mid": v(71.32, 71.32) * mm, "end": v(64.25, 74.25) * mm});
            skCircle(sketch, "E79.8", {"center": v(60, 60) * mm, "radius": 4 * mm});
            skArc(sketch, "E79.9", {"start": v(60, 38.83) * mm, "mid": v(58.44, 44.2) * mm, "end": v(54.26, 47.88) * mm});
            skArc(sketch, "E79.10", {"start": v(54.26, 47.88) * mm, "mid": v(0, 60) * mm, "end": v(-54.26, 47.88) * mm});
            skArc(sketch, "E79.11", {"start": v(-54.26, 47.88) * mm, "mid": v(-58.44, 44.2) * mm, "end": v(-60, 38.83) * mm});
            skLineSegment(sketch, "E79.12", {"start": v(-60, 38.83) * mm, "end": v(-60, -38.83) * mm});
            skArc(sketch, "E79.13", {"start": v(-60, -38.83) * mm, "mid": v(-58.44, -44.2) * mm, "end": v(-54.26, -47.88) * mm});
            skArc(sketch, "E79.14", {"start": v(-54.26, -47.88) * mm, "mid": v(0, -60) * mm, "end": v(54.26, -47.88) * mm});
            skArc(sketch, "E79.15", {"start": v(54.26, -47.88) * mm, "mid": v(58.44, -44.2) * mm, "end": v(60, -38.83) * mm});
            skLineSegment(sketch, "E79.16", {"start": v(60, 38.83) * mm, "end": v(60, -38.83) * mm});
            skCircle(sketch, "E79.17", {"center": v(-60, 60) * mm, "radius": 4 * mm});
            skCircle(sketch, "E79.18", {"center": v(-60, -60) * mm, "radius": 4 * mm});
            skCircle(sketch, "E79.19", {"center": v(60, -60) * mm, "radius": 4 * mm});
            skLineSegment(sketch, "E80", {"start": v(0, 104.25) * mm, "end": v(0, 74.25) * mm, "construction": true});
            skCircle(sketch, "E81", {"center": v(0, 104.25) * mm, "radius": 6 * mm});
            skLineSegment(sketch, "E82", {"start": v(-33, 74.25) * mm, "end": v(-15, 92.25) * mm});
            skLineSegment(sketch, "E83", {"start": v(-15, 92.25) * mm, "end": v(-15, 104.25) * mm});
            skLineSegment(sketch, "E84", {"start": v(15, 104.25) * mm, "end": v(15, 92.25) * mm});
            skLineSegment(sketch, "E85", {"start": v(15, 92.25) * mm, "end": v(33, 74.25) * mm});
            skArc(sketch, "E86", {"start": v(15, 104.25) * mm, "mid": v(0, 119.25) * mm, "end": v(-15, 104.25) * mm});
            skLineSegment(sketch, "E87", {"start": v(-74.25, 0) * mm, "end": v(74.25, 0) * mm, "construction": true});
            skLineSegment(sketch, "E88.MirrorCS", {"start": v(15, -92.25) * mm, "end": v(33, -74.25) * mm});
            skLineSegment(sketch, "E89.MirrorCS", {"start": v(15, -104.25) * mm, "end": v(15, -92.25) * mm});
            skArc(sketch, "E90.MirrorCS", {"start": v(15, -104.25) * mm, "mid": v(0, -119.25) * mm, "end": v(-15, -104.25) * mm});
            skCircle(sketch, "E91.MirrorC", {"center": v(0, -104.25) * mm, "radius": 6 * mm});
            skLineSegment(sketch, "E92.MirrorCS", {"start": v(-33, -74.25) * mm, "end": v(-15, -92.25) * mm});
            skLineSegment(sketch, "E93.MirrorCS", {"start": v(-15, -92.25) * mm, "end": v(-15, -104.25) * mm});
            skSolve(sketch);
        }
        {
            var Q0;
            Q0 = qSketchRegion(id + "F16", true);
            var Q1;
            Q1=makeQuery(id+"F2.opExtrude","CAP_FACE",FACE,{"disambiguationData":[OSD([sQuery(id+"F0.wireOp",EDGE,"E12"),sQuery(id+"F0.wireOp",EDGE,"E13"),sQuery(id+"F0.wireOp",EDGE,"E14"),sQuery(id+"F0.wireOp",EDGE,"E15"),sQuery(id+"F0.wireOp",EDGE,"E17.filletArc"),sQuery(id+"F0.wireOp",EDGE,"E18.filletArc"),sQuery(id+"F0.wireOp",EDGE,"E19.filletArc"),sQuery(id+"F0.wireOp",EDGE,"E20.filletArc"),sQuery(id+"F0.wireOp",EDGE,"E25.0"),sQuery(id+"F0.wireOp",EDGE,"E25.1"),sQuery(id+"F0.wireOp",EDGE,"E25.2"),sQuery(id+"F0.wireOp",EDGE,"E25.3"),sQuery(id+"F0.wireOp",EDGE,"E25.4"),sQuery(id+"F0.wireOp",EDGE,"E25.5"),sQuery(id+"F0.wireOp",EDGE,"E25.6"),sQuery(id+"F0.wireOp",EDGE,"E25.7")])],"isStart":false});
            extrude(context, id + "F17", {"entities" : qUnion([Q0]), "endBound" : BoundingType.UP_TO_SURFACE, "endBoundEntityFace" : qUnion([Q1]), "depth" : 25 * mm});
        }
    });
